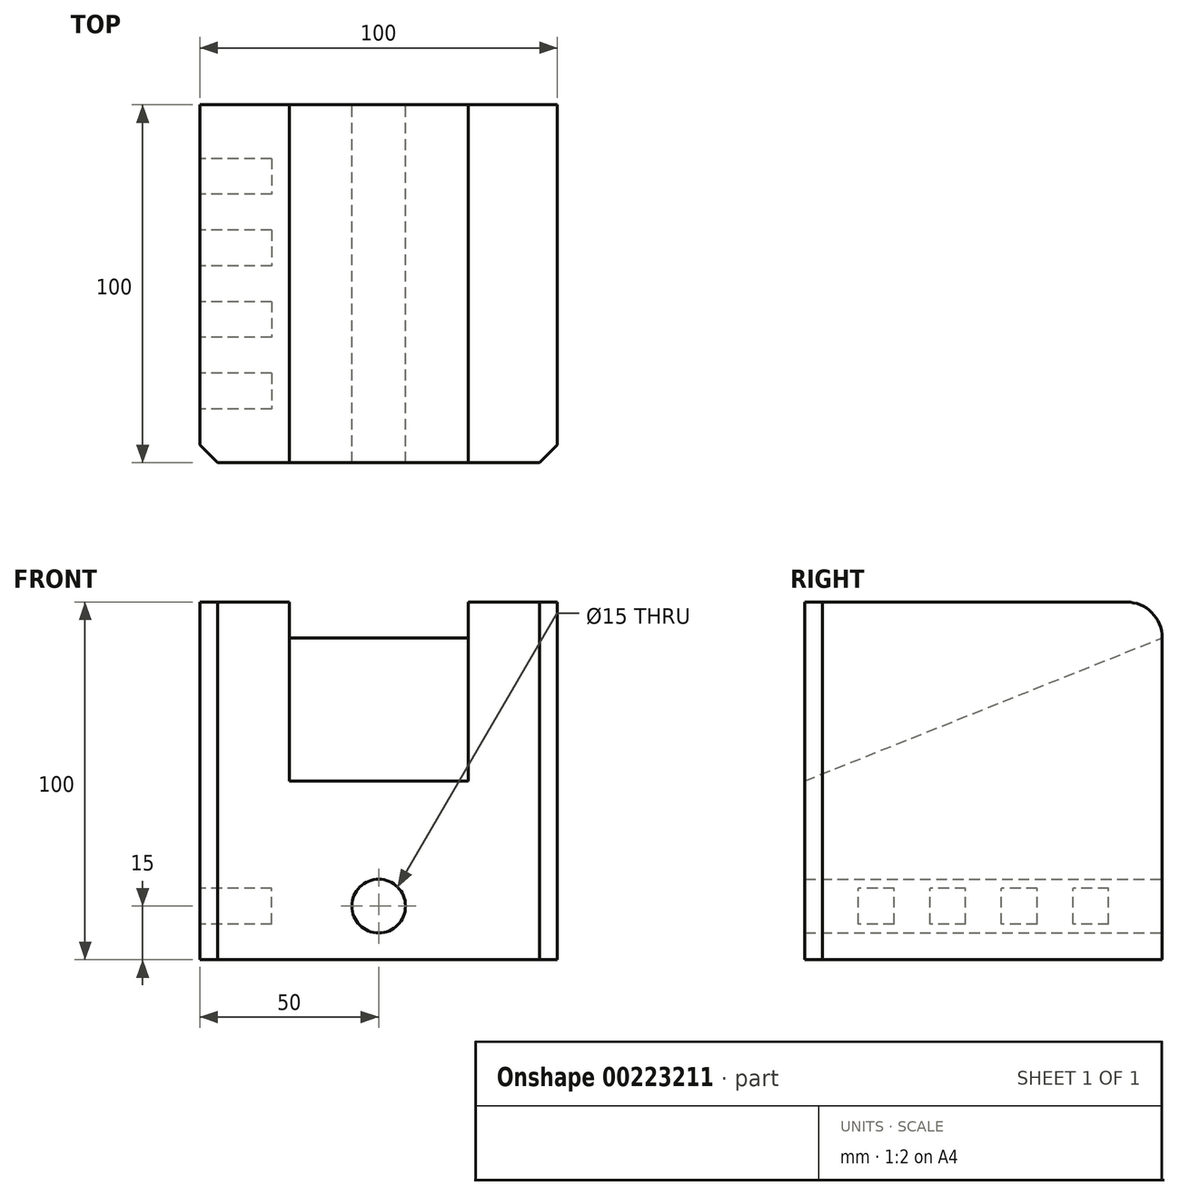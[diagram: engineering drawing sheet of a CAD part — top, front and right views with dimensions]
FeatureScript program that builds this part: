
annotation { "Feature Type Name" : "Feature", "Feature Type Description" : "" }
export const myFeature = defineFeature(function(context is Context, id is Id, definition is map)
    precondition{}
    {
        {
            var Q0;
            Q0=qCreatedBy(makeId("Front.planeOp"),FACE);
            var sketch = newSketch(context, id + "F0", { "sketchPlane" : qUnion([Q0])});
            skLineSegment(sketch, "E0.bottom", {"start": v(0, 0) * mm, "end": v(100, 0) * mm});
            skLineSegment(sketch, "E0.top", {"start": v(0, 100) * mm, "end": v(100, 100) * mm});
            skLineSegment(sketch, "E0.left", {"start": v(0, 0) * mm, "end": v(0, 100) * mm});
            skLineSegment(sketch, "E0.right", {"start": v(100, 0) * mm, "end": v(100, 100) * mm});
            skCircle(sketch, "E1", {"center": v(50, 15) * mm, "radius": 7.5 * mm});
            skSolve(sketch);
        }
        {
            var Q0;
            Q0 = qSketchRegion(id + "F0", true);
            extrude(context, id + "F1", {"entities" : qUnion([Q0]), "depth" : 100 * mm});
        }
        {
            var Q0;
            Q0=makeQuery(id+"F1.opExtrude","SWEPT_FACE",FACE,{"disambiguationData":[OSD([sQuery(id+"F0.wireOp",EDGE,"E0.right")])]});
            var Q1;
            Q1=makeQuery(id+"F1.opExtrude","SWEPT_FACE",FACE,{"disambiguationData":[OSD([sQuery(id+"F0.wireOp",EDGE,"E0.left")])]});
            cPlane(context, id + "F2", {"entities" : qUnion([Q0, Q1]), "cplaneType" : CPlaneType.MID_PLANE, "offset" : 25 * mm, "width" : 150 * mm, "height" : 150 * mm});
        }
        {
            var Q0;
            Q0=qCreatedBy(id+"F2.planeOp",FACE);
            var sketch = newSketch(context, id + "F3", { "sketchPlane" : qUnion([Q0])});
            skLineSegment(sketch, "E2", {"start": v(0, 0) * mm, "end": v(0, 90) * mm, "construction": true});
            skLineSegment(sketch, "E3", {"start": v(0, 90) * mm, "end": v(0, 100) * mm});
            skLineSegment(sketch, "E4", {"start": v(0, 100) * mm, "end": v(-100, 100) * mm});
            skLineSegment(sketch, "E5", {"start": v(-100, 100) * mm, "end": v(-100, 50) * mm});
            skLineSegment(sketch, "E6", {"start": v(-100, 50) * mm, "end": v(0, 90) * mm});
            skSolve(sketch);
        }
        {
            var Q0;
            Q0 = qSketchRegion(id + "F3", true);
            extrude(context, id + "F4", {"entities" : qUnion([Q0]), "operationType" : NewBodyOperationType.REMOVE, "endBound" : BoundingType.SYMMETRIC, "oppositeDirection" : true, "depth" : 50 * mm});
        }
        {
            var Q0;
            {var subQ0=sQuery(id+"F0.wireOp",EDGE,"E0.left");var subQ1=sQuery(id+"F0.wireOp",EDGE,"E0.top");Q0=makeQuery(id+"F4.boolean.opBoolean","SPLIT",EDGE,{"disambiguationData":[TD([makeQuery(id+"F1.opExtrude","SWEPT_FACE",FACE,{"disambiguationData":[OSD([subQ0])]})])],"derivedFrom":makeQuery(id+"F1.opExtrude","CAP_EDGE",EDGE,{"disambiguationData":[OSD([subQ1])],"isStart":true})});}
            var Q1;
            {var subQ0=sQuery(id+"F0.wireOp",EDGE,"E0.right");var subQ1=sQuery(id+"F0.wireOp",EDGE,"E0.top");Q1=makeQuery(id+"F4.boolean.opBoolean","SPLIT",EDGE,{"disambiguationData":[TD([makeQuery(id+"F1.opExtrude","SWEPT_FACE",FACE,{"disambiguationData":[OSD([subQ0])]})])],"derivedFrom":makeQuery(id+"F1.opExtrude","CAP_EDGE",EDGE,{"disambiguationData":[OSD([subQ1])],"isStart":true})});}
            fillet(context, id + "F5", {"entities" : qUnion([Q0, Q1]), "radius" : 10 * mm, "tangentPropagation" : true, "allowEdgeOverflow" : false});
        }
        {
            var Q0;
            Q0=makeQuery(id+"F1.opExtrude","CAP_EDGE",EDGE,{"disambiguationData":[OSD([sQuery(id+"F0.wireOp",EDGE,"E0.right")])],"isStart":false});
            var Q1;
            Q1=makeQuery(id+"F1.opExtrude","CAP_EDGE",EDGE,{"disambiguationData":[OSD([sQuery(id+"F0.wireOp",EDGE,"E0.left")])],"isStart":false});
            chamfer(context, id + "F6", {"entities" : qUnion([Q0, Q1]), "width" : 5 * mm, "tangentPropagation" : true});
        }
        {
            var Q0;
            Q0=qCreatedBy(makeId("Right.planeOp"),FACE);
            var sketch = newSketch(context, id + "F7", { "sketchPlane" : qUnion([Q0])});
            skLineSegment(sketch, "E7.bottom", {"start": v(-15, 10) * mm, "end": v(-25, 10) * mm});
            skLineSegment(sketch, "E7.top", {"start": v(-15, 20) * mm, "end": v(-25, 20) * mm});
            skLineSegment(sketch, "E7.left", {"start": v(-15, 10) * mm, "end": v(-15, 20) * mm});
            skLineSegment(sketch, "E7.right", {"start": v(-25, 10) * mm, "end": v(-25, 20) * mm});
            skLineSegment(sketch, "E8.1.0.0", {"start": v(-35, 20) * mm, "end": v(-45, 20) * mm});
            skLineSegment(sketch, "E8.1.0.1", {"start": v(-45, 10) * mm, "end": v(-45, 20) * mm});
            skLineSegment(sketch, "E8.1.0.2", {"start": v(-35, 10) * mm, "end": v(-45, 10) * mm});
            skLineSegment(sketch, "E8.1.0.3", {"start": v(-35, 10) * mm, "end": v(-35, 20) * mm});
            skLineSegment(sketch, "E8.2.0.0", {"start": v(-55, 20) * mm, "end": v(-65, 20) * mm});
            skLineSegment(sketch, "E8.2.0.1", {"start": v(-65, 10) * mm, "end": v(-65, 20) * mm});
            skLineSegment(sketch, "E8.2.0.2", {"start": v(-55, 10) * mm, "end": v(-65, 10) * mm});
            skLineSegment(sketch, "E8.2.0.3", {"start": v(-55, 10) * mm, "end": v(-55, 20) * mm});
            skLineSegment(sketch, "E8.3.0.0", {"start": v(-75, 20) * mm, "end": v(-85, 20) * mm});
            skLineSegment(sketch, "E8.3.0.1", {"start": v(-85, 10) * mm, "end": v(-85, 20) * mm});
            skLineSegment(sketch, "E8.3.0.2", {"start": v(-75, 10) * mm, "end": v(-85, 10) * mm});
            skLineSegment(sketch, "E8.3.0.3", {"start": v(-75, 10) * mm, "end": v(-75, 20) * mm});
            skLineSegment(sketch, "E8.direction1", {"start": v(-25, 20) * mm, "end": v(-45, 20) * mm, "construction": true});
            skSolve(sketch);
        }
        {
            var Q0;
            Q0 = qSketchRegion(id + "F7", true);
            extrude(context, id + "F8", {"entities" : qUnion([Q0]), "operationType" : NewBodyOperationType.REMOVE, "depth" : 20 * mm});
        }
    });
